# Revit family: PRD_FrankeWS_WlHngWshBsns_AnimaWashbasin_ANMX502
name_source: partatom
category: Plumbing Fixtures
revit_build: Autodesk Revit 2018 (Build: 20190510_1515(x64)
units: mm (PartAtom-declared; Revit-internal decimal feet)

## family parameters
Cut with Voids When Loaded = No
Host = Face
OmniClass Number = 23.45.05.14.14
OmniClass Title = Sinks/Lavatories
Part Type = Normal
Room Calculation Point = No
Round Connector Dimension = Use Diameter
Shared = No

## types (1)
- ANMX502
    AssetType = Fixed
    BIMObjectName = PRD_AR_WallHungWashBasins_AnimaWashbasin_ANMX502
    Category = Pr_40_20_96_96, Wall-hung wash basins
    Color = Stainless steel
    Default Elevation = 850 mm  [stored 2.78871 ft]
    Description = Single wash stand for wall-mounting, chrome-nickel steel, surface silk matt, material 1.5 mm thick, barrier-free wash stand in acc. with SIA 500, seamlessly welded round basin, basin diameter of 350 mm, rectangular wash stand shape with front corners rounded, no bank of fittings, seamlessly integrated plug strainer and drainpipe DN 32, siphon mounted under plaster, not included, integrated and reinforced assembly panel measuring 280 mm, including stainless steel screws and rawl plugs.Dimensions 500 x 132 x 400 mm (W x H x D)
    DrainSize = DN-32
    DurationUnit = year
    Features = stainless steel, 1.50 mm, 500 x 132 x 400 mm (W x H x D)
    Finish = Satin finished
    Form = Wall hung wash basin
    GrossWeight = 6.20 kg
    IfcExportAs = IfcSanitaryTerminalType
    IfcExportType = WASHHANDBASIN
    IntegralAccessories = Incl. stainless steel screws and rawl plugs
    Manufacturer = KWC Group AG
    ManufacturerName = KWC Group AG
    ManufacturerURL = www.kwc.com
    Material = Stainless steel
    MaterialsBody = Stainless steel 1.4301
    MaterialsFinishAndColour = Stainless steel
    Model = ANMX502
    ModelNumber = 2030029755
    ModelReference = ANMX502
    NBSDescription = Wall hung wash basins
    NBSReference = 45-35-70/369
    Name = ANIMA wall-hung wash basin ANMX502
    NetWeight = 6.00 kg
    NominalDepth = 400 mm  [stored 1.31234 ft]
    NominalHeight = 132 mm  [stored 0.433071 ft]
    NominalLength = 0 mm  [stored 0 ft]
    NominalWidth = 500 mm  [stored 1.64042 ft]
    ProductInformation = https://pim.kwc.com
    Shape = Rectangular
    Size = 500 x 400 x 132 mm
    URL = www.kwc.com
    Uniclass2015Code = Pr_40_20_96_96
    Uniclass2015Title = Wall-hung wash basins
    Uniclass2015Version = Products v1.5
    Version = 1
    WarrantyDurationUnit = year
    WashHandBasinMounting = WallHung
    WashHandBasinType = HandRinse
    WashbasinMaterial = PRD_AR_StainlessSteel_SatinFinished
    WasteSize = 32
    WaterSupplyOverflowAndWasteHolesOverflow = None
    WaterSupplyOverflowAndWasteHolesWaste = Center-Center
    WaterSupplyOverflowAndWasteHolesWaterSupply = No tapholes

note: [stored X ft] marks values corroborated as IEEE doubles in the binary element streams (Revit-internal decimal feet)

## geometry (parser evidence)
native form markers: Sweep x6
no freeform markers — native parametric forms only
